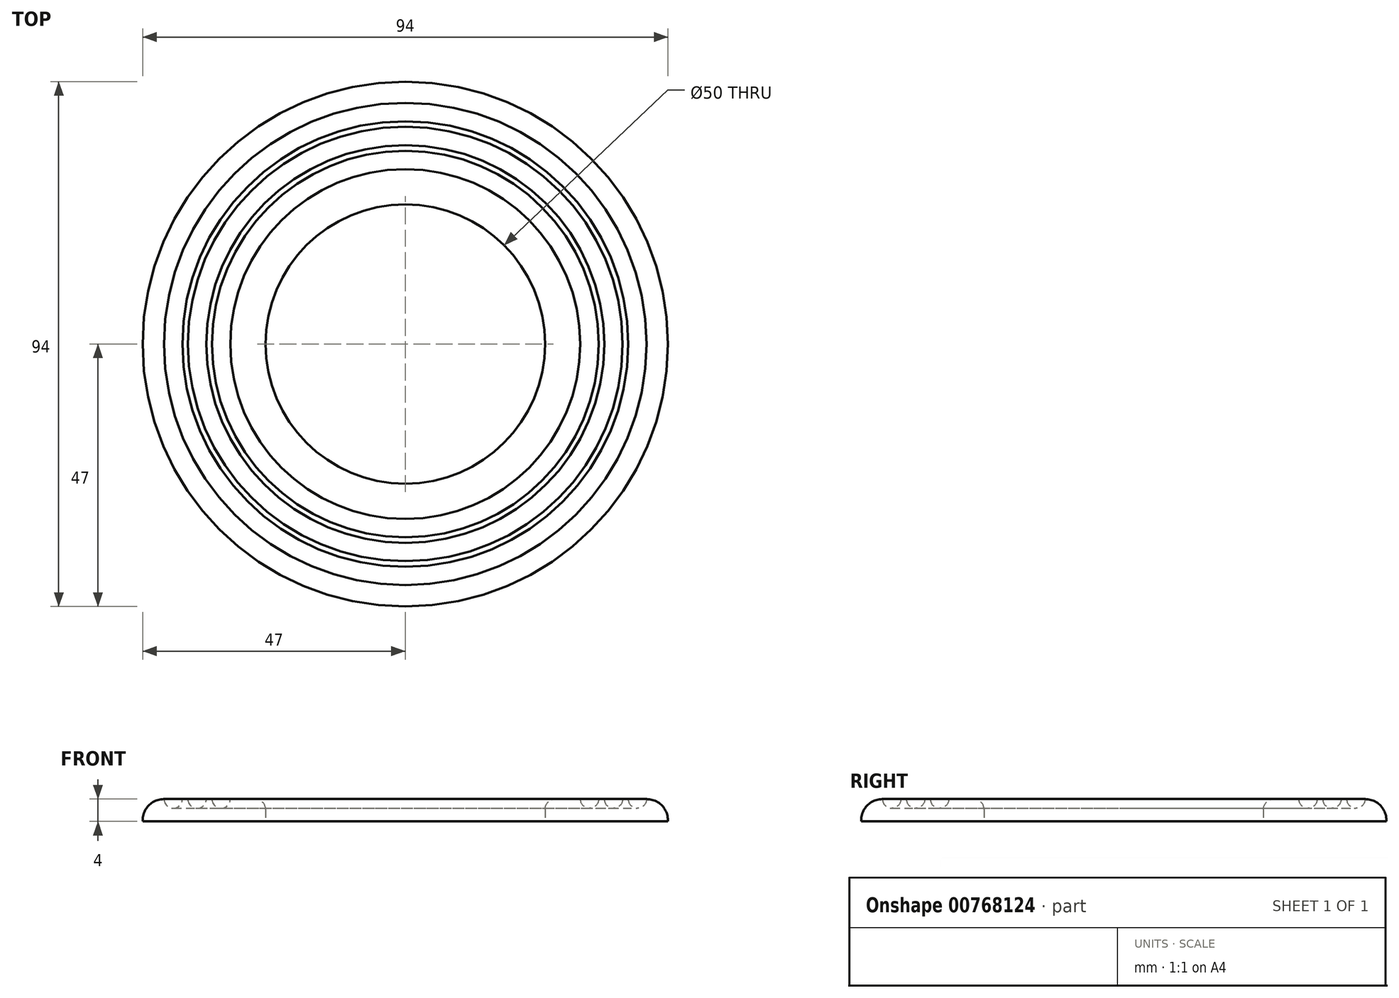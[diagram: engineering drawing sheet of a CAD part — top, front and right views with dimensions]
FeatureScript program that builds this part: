
annotation { "Feature Type Name" : "Feature", "Feature Type Description" : "" }
export const myFeature = defineFeature(function(context is Context, id is Id, definition is map)
    precondition{}
    {
        {
            var Q0;
            Q0=qCreatedBy(makeId("Front.planeOp"),FACE);
            var sketch = newSketch(context, id + "F0", { "sketchPlane" : qUnion([Q0])});
            skLineSegment(sketch, "E0", {"start": v(-25, 0) * mm, "end": v(-47, 0) * mm});
            skLineSegment(sketch, "E1", {"start": v(-47, 0) * mm, "end": v(-47, 0.2) * mm});
            skLineSegment(sketch, "E2", {"start": v(-43.2, 4) * mm, "end": v(-43.18, 4) * mm});
            skLineSegment(sketch, "E3", {"start": v(-25, 2.15) * mm, "end": v(-25, 0) * mm});
            skLineSegment(sketch, "E4", {"start": v(0, 0) * mm, "end": v(0, 4) * mm});
            skPoint(sketch, "E5.visualSharp", {"position": v(-47, 4) * mm});
            skArc(sketch, "E5.filletArc", {"start": v(-43.2, 4) * mm, "mid": v(-45.89, 2.89) * mm, "end": v(-47, 0.2) * mm});
            skPoint(sketch, "E6.visualSharp", {"position": v(-25, 4) * mm});
            skArc(sketch, "E6.filletArc", {"start": v(-25, 2.15) * mm, "mid": v(-25.54, 3.46) * mm, "end": v(-26.85, 4) * mm});
            skArc(sketch, "E7", {"start": v(-43.18, 4) * mm, "mid": v(-41.54, 2.36) * mm, "end": v(-39.9, 4) * mm});
            skLineSegment(sketch, "E8.trimOffspring", {"start": v(-35.6, 4) * mm, "end": v(-34.6, 4) * mm});
            skLineSegment(sketch, "E9", {"start": v(-39.9, 4) * mm, "end": v(-38.9, 4) * mm});
            skArc(sketch, "E10", {"start": v(-38.9, 4) * mm, "mid": v(-37.25, 2.36) * mm, "end": v(-35.6, 4) * mm});
            skArc(sketch, "E11", {"start": v(-34.6, 4) * mm, "mid": v(-32.96, 2.36) * mm, "end": v(-31.32, 4) * mm});
            skLineSegment(sketch, "E12.trimOffspring", {"start": v(-31.32, 4) * mm, "end": v(-26.85, 4) * mm});
            skSolve(sketch);
        }
        {
            var Q0;
            Q0=makeQuery(id+"F0.imprint","IMPRINT",FACE,{"disambiguationData":[TD([[makeQuery(id+"F0.imprint","IMPRINT",EDGE,{"derivedFrom":sQuery(id+"F0.wireOp",EDGE,"E0")}),-1.0]])]});
            var Q1;
            Q1=sQuery(id+"F0.wireOp",EDGE,"E4");
            revolve(context, id + "F1", {"surfaceOperationType" : NewSurfaceOperationType.NEW, "entities" : qUnion([Q0]), "axis" : qUnion([Q1]), "revolveType" : RevolveType.FULL});
        }
    });
